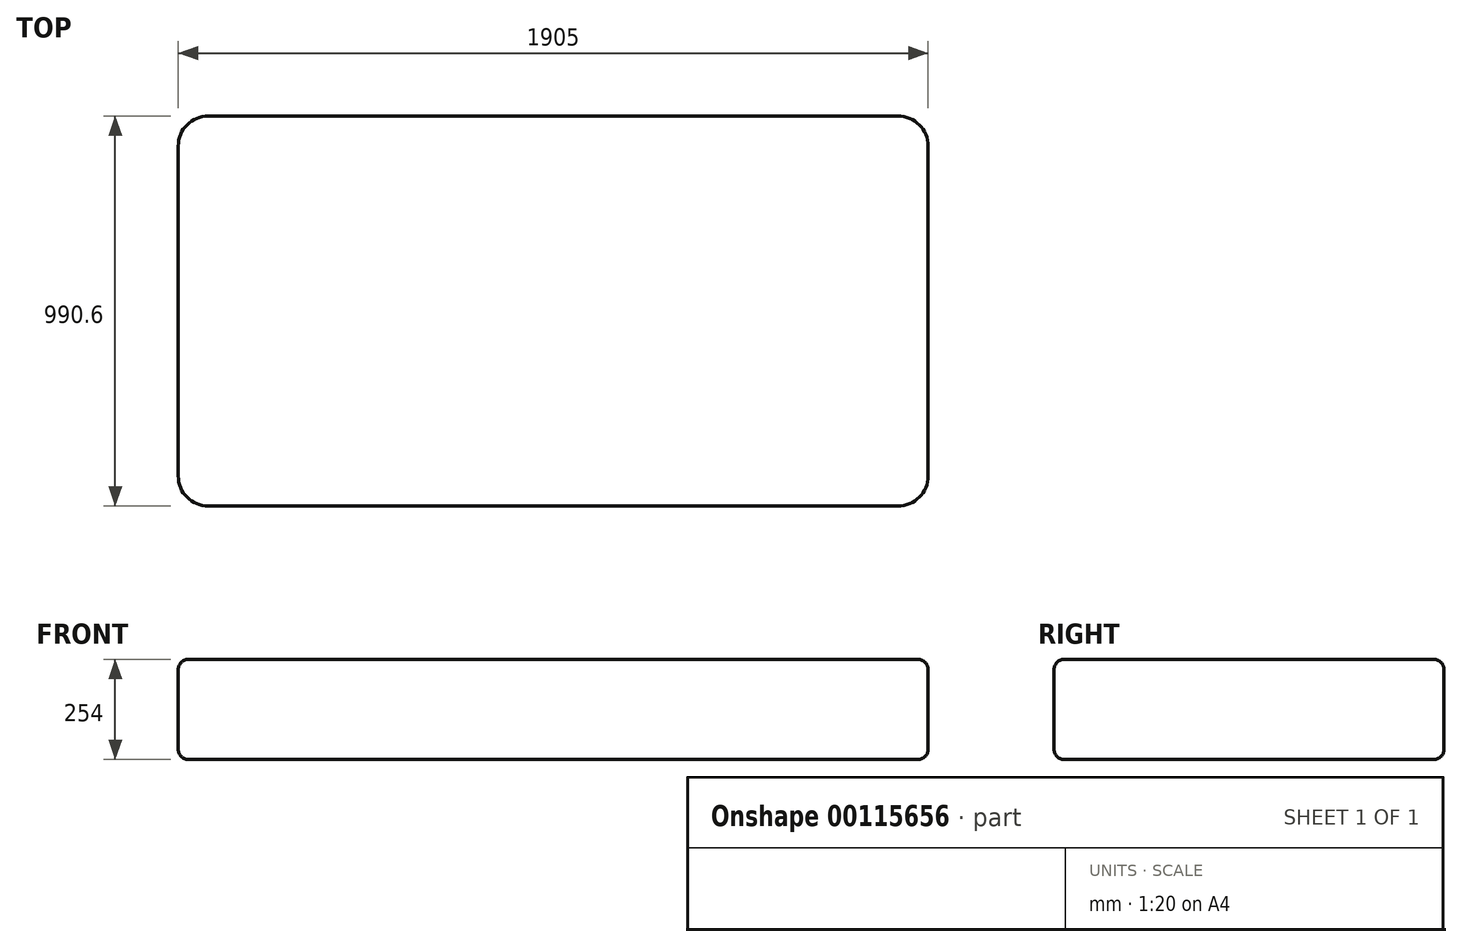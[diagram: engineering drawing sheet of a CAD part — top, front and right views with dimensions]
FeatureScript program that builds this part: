
annotation { "Feature Type Name" : "Feature", "Feature Type Description" : "" }
export const myFeature = defineFeature(function(context is Context, id is Id, definition is map)
    precondition{}
    {
        {
            var Q0;
            Q0=qCreatedBy(makeId("Top.planeOp"),FACE);
            var sketch = newSketch(context, id + "F0", { "sketchPlane" : qUnion([Q0])});
            skLineSegment(sketch, "E0.bottom", {"start": v(876.3, 495.3) * mm, "end": v(-876.3, 495.3) * mm});
            skLineSegment(sketch, "E0.top", {"start": v(876.3, -495.3) * mm, "end": v(-876.3, -495.3) * mm});
            skLineSegment(sketch, "E0.left", {"start": v(952.5, 419.1) * mm, "end": v(952.5, -419.1) * mm});
            skLineSegment(sketch, "E0.right", {"start": v(-952.5, 419.1) * mm, "end": v(-952.5, -419.1) * mm});
            skPoint(sketch, "E0.middle", {"position": v(0, 0) * mm});
            skPoint(sketch, "E1.visualSharp", {"position": v(-952.5, -495.3) * mm});
            skArc(sketch, "E1.filletArc", {"start": v(-952.5, -419.1) * mm, "mid": v(-930.18, -472.98) * mm, "end": v(-876.3, -495.3) * mm});
            skPoint(sketch, "E2.visualSharp", {"position": v(952.5, -495.3) * mm});
            skArc(sketch, "E2.filletArc", {"start": v(876.3, -495.3) * mm, "mid": v(930.18, -472.98) * mm, "end": v(952.5, -419.1) * mm});
            skPoint(sketch, "E3.visualSharp", {"position": v(952.5, 495.3) * mm});
            skArc(sketch, "E3.filletArc", {"start": v(952.5, 419.1) * mm, "mid": v(930.18, 472.98) * mm, "end": v(876.3, 495.3) * mm});
            skPoint(sketch, "E4.visualSharp", {"position": v(-952.5, 495.3) * mm});
            skArc(sketch, "E4.filletArc", {"start": v(-876.3, 495.3) * mm, "mid": v(-930.18, 472.98) * mm, "end": v(-952.5, 419.1) * mm});
            skSolve(sketch);
        }
        {
            var Q0;
            Q0 = qSketchRegion(id + "F0", true);
            extrude(context, id + "F1", {"entities" : qUnion([Q0]), "flatOperationType" : FlatOperationType.REMOVE, "offsetDistance" : 25.4 * mm, "depth" : 254 * mm, "domain" : OperationDomain.MODEL});
        }
        {
            var Q0;
            Q0=makeQuery(id+"F1.opExtrude","CAP_EDGE",EDGE,{"disambiguationData":[OSD([sQuery(id+"F0.wireOp",EDGE,"E0.top")])],"isStart":false});
            var Q1;
            Q1=makeQuery(id+"F1.opExtrude","CAP_EDGE",EDGE,{"disambiguationData":[OSD([sQuery(id+"F0.wireOp",EDGE,"E0.top")])],"isStart":true});
            fillet(context, id + "F2", {"entities" : qUnion([Q0, Q1]), "radius" : 25.4 * mm, "tangentPropagation" : true, "allowEdgeOverflow" : false});
        }
    });
